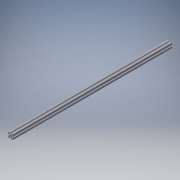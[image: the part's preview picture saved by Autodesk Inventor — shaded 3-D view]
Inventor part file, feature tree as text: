
AUTODESK INVENTOR PART (.ipt)
format: ipt  version: 2016 SP1 (Build 200210100, 210)  size: 227,840 bytes
history: native  units: mm (DEFAULTED — no unit token found)
features: other x4, extrude x1, sketch x1
ambient origin geometry x8: Origin, YZ Plane, XZ Plane, XY Plane, X Axis, Y Axis, Z Axis, Center Point
bodies: Solid1 (feature_tree)
feature tree (6):
  other  "Table"
  other  "30x30-01"
  other  "30x30-02"
  other  "30x30-03"
  extrude  "Extrusion1"  [1 undecoded]
  sketch  "Sketch1"  dims[d3=0.0mm]
note: 1 required parameter value undecoded (feature->parameter linkage not recoverable at this tier; creation-order binding heuristic only, values carry confidence <= 0.55)
